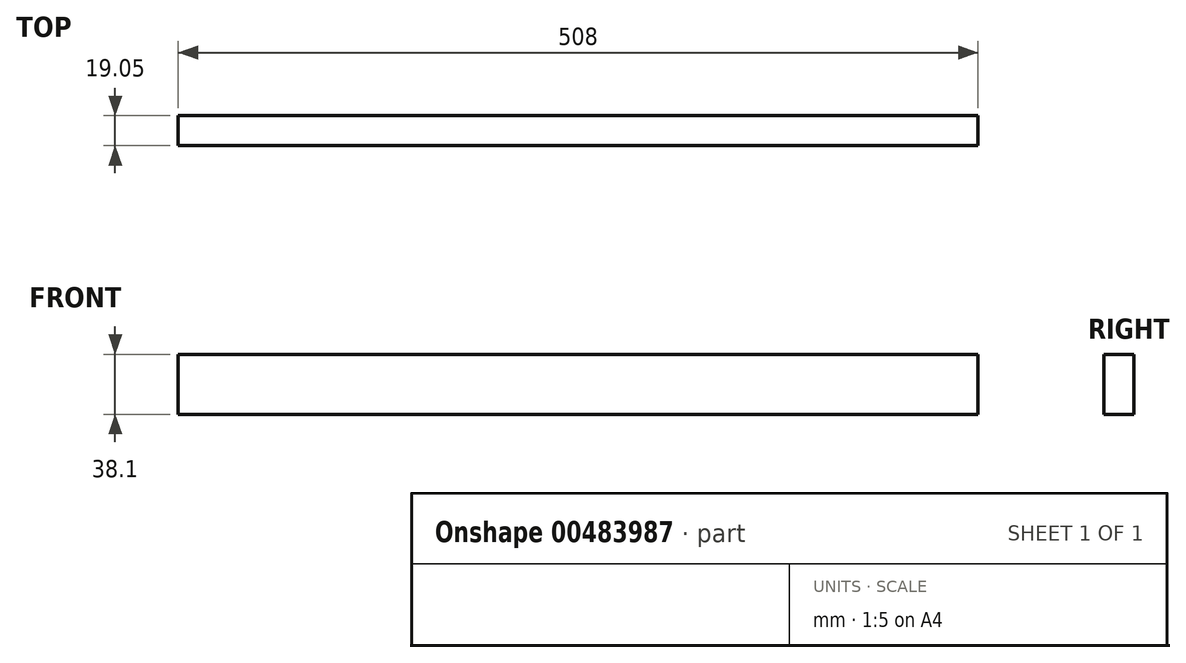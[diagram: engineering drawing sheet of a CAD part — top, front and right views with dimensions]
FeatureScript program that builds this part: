
annotation { "Feature Type Name" : "Feature", "Feature Type Description" : "" }
export const myFeature = defineFeature(function(context is Context, id is Id, definition is map)
    precondition{}
    {
        {
            var Q0;
            Q0=qCreatedBy(makeId("Front.planeOp"),FACE);
            var sketch = newSketch(context, id + "F0", { "sketchPlane" : qUnion([Q0])});
            skLineSegment(sketch, "E0.bottom", {"start": v(254, -19.05) * mm, "end": v(-254, -19.05) * mm});
            skLineSegment(sketch, "E0.top", {"start": v(254, 19.05) * mm, "end": v(-254, 19.05) * mm});
            skLineSegment(sketch, "E0.left", {"start": v(254, -19.05) * mm, "end": v(254, 19.05) * mm});
            skLineSegment(sketch, "E0.right", {"start": v(-254, -19.05) * mm, "end": v(-254, 19.05) * mm});
            skPoint(sketch, "E0.middle", {"position": v(0, 0) * mm});
            skSolve(sketch);
        }
        {
            var Q0;
            Q0=qSketchRegion(id+"F0",true);
            extrude(context, id + "F1", {"entities" : qUnion([Q0]), "depth" : 19.05 * mm});
        }
    });
